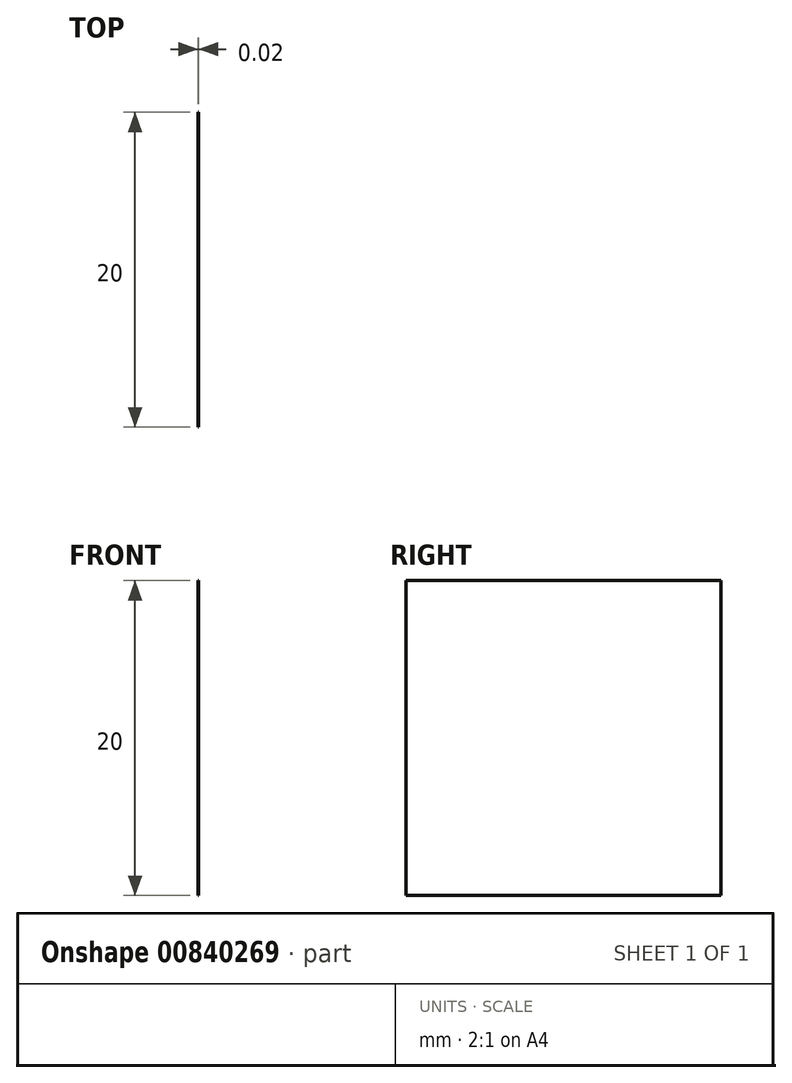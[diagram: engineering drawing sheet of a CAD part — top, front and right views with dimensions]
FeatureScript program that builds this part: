
annotation { "Feature Type Name" : "Feature", "Feature Type Description" : "" }
export const myFeature = defineFeature(function(context is Context, id is Id, definition is map)
    precondition{}
    {
        {
            var Q0;
            Q0=qCreatedBy(makeId("Right.planeOp"),FACE);
            var sketch = newSketch(context, id + "F0", { "sketchPlane" : qUnion([Q0])});
            skLineSegment(sketch, "E0.bottom", {"start": v(0, 0) * mm, "end": v(20, 0) * mm});
            skLineSegment(sketch, "E0.top", {"start": v(0, -20) * mm, "end": v(20, -20) * mm});
            skLineSegment(sketch, "E0.left", {"start": v(0, 0) * mm, "end": v(0, -20) * mm});
            skLineSegment(sketch, "E0.right", {"start": v(20, 0) * mm, "end": v(20, -20) * mm});
            skSolve(sketch);
        }
        {
            var Q0;
            Q0=makeQuery(id+"F0.imprint","IMPRINT",FACE,{"disambiguationData":[TD([[makeQuery(id+"F0.imprint","IMPRINT",EDGE,{"derivedFrom":sQuery(id+"F0.wireOp",EDGE,"E0.bottom")}),-1.0]])]});
            extrude(context, id + "F1", {"entities" : qUnion([Q0]), "depth" : 0.02 * mm, "offsetDistance" : 25 * mm});
        }
    });
